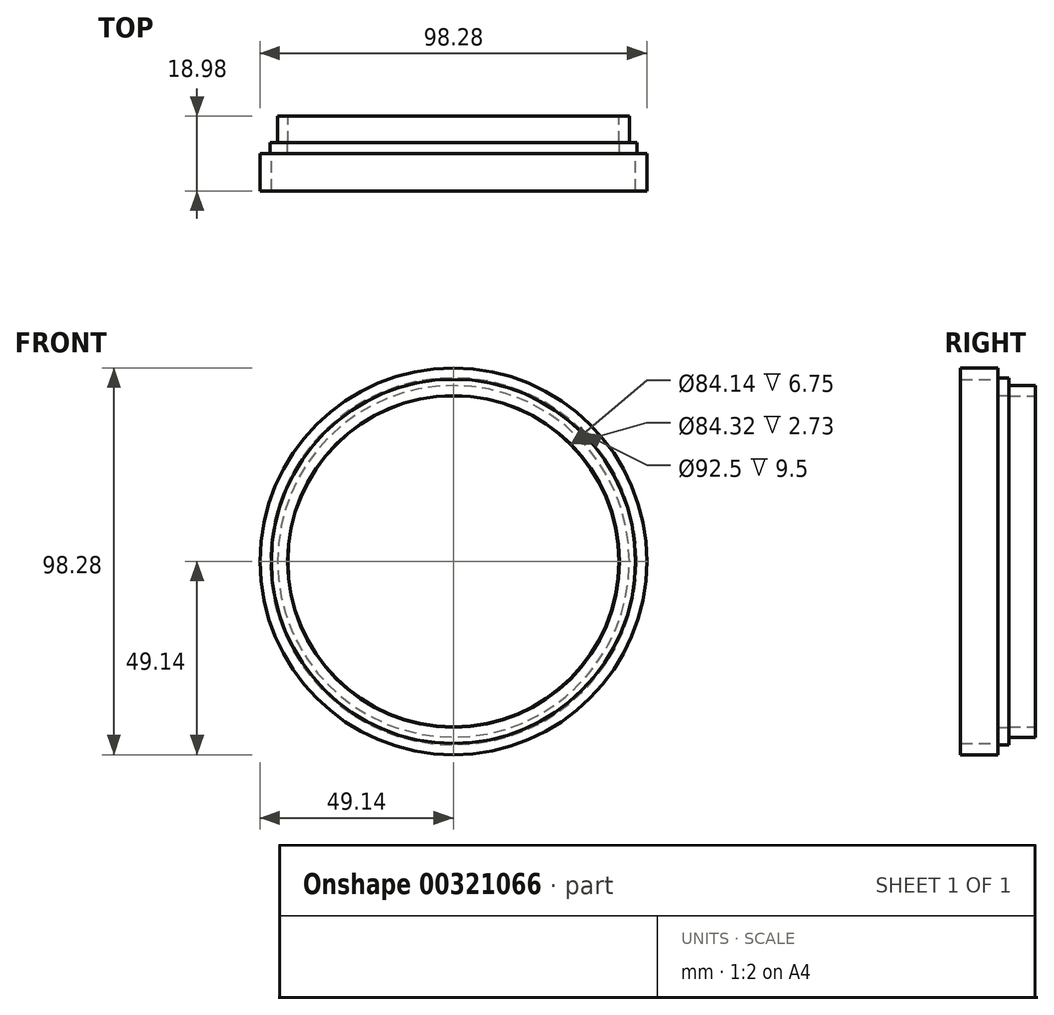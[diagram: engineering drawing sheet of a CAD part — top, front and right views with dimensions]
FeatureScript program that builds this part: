
annotation { "Feature Type Name" : "Feature", "Feature Type Description" : "" }
export const myFeature = defineFeature(function(context is Context, id is Id, definition is map)
    precondition{}
    {
        {
            var Q0;
            Q0=qCreatedBy(makeId("Front.planeOp"),FACE);
            var sketch = newSketch(context, id + "F0", { "sketchPlane" : qUnion([Q0])});
            skCircle(sketch, "E0", {"center": v(0, 0) * mm, "radius": 42.07 * mm});
            skCircle(sketch, "E1", {"center": v(0, 0) * mm, "radius": 44.67 * mm});
            skSolve(sketch);
        }
        {
            var Q0;
            Q0 = qSketchRegion(id + "F0", true);
            extrude(context, id + "F1", {"entities" : qUnion([Q0]), "depth" : 6.75 * mm});
        }
        {
            var Q0;
            Q0=makeQuery(id+"F1.opExtrude","CAP_FACE",FACE,{"disambiguationData":[OSD([sQuery(id+"F0.wireOp",EDGE,"E0"),sQuery(id+"F0.wireOp",EDGE,"E1")])],"isStart":false});
            var sketch = newSketch(context, id + "F2", { "sketchPlane" : qUnion([Q0])});
            skCircle(sketch, "E2", {"center": v(0, 0) * mm, "radius": 42.16 * mm});
            skCircle(sketch, "E3", {"center": v(0, 0) * mm, "radius": 46.62 * mm});
            skSolve(sketch);
        }
        {
            var Q0;
            Q0 = qSketchRegion(id + "F2", true);
            extrude(context, id + "F3", {"entities" : qUnion([Q0]), "operationType" : NewBodyOperationType.ADD, "depth" : 2.73 * mm});
        }
        {
            var Q0;
            Q0=makeQuery(id+"F3.opExtrude","CAP_FACE",FACE,{"disambiguationData":[OSD([sQuery(id+"F2.wireOp",EDGE,"E2"),sQuery(id+"F2.wireOp",EDGE,"E3")])],"isStart":false});
            var sketch = newSketch(context, id + "F4", { "sketchPlane" : qUnion([Q0])});
            skCircle(sketch, "E4", {"center": v(0, 0) * mm, "radius": 49.14 * mm});
            skCircle(sketch, "E5", {"center": v(0, 0) * mm, "radius": 46.25 * mm});
            skSolve(sketch);
        }
        {
            var Q0;
            Q0 = qSketchRegion(id + "F4", true);
            extrude(context, id + "F5", {"entities" : qUnion([Q0]), "operationType" : NewBodyOperationType.ADD, "depth" : 9.5 * mm});
        }
    });
